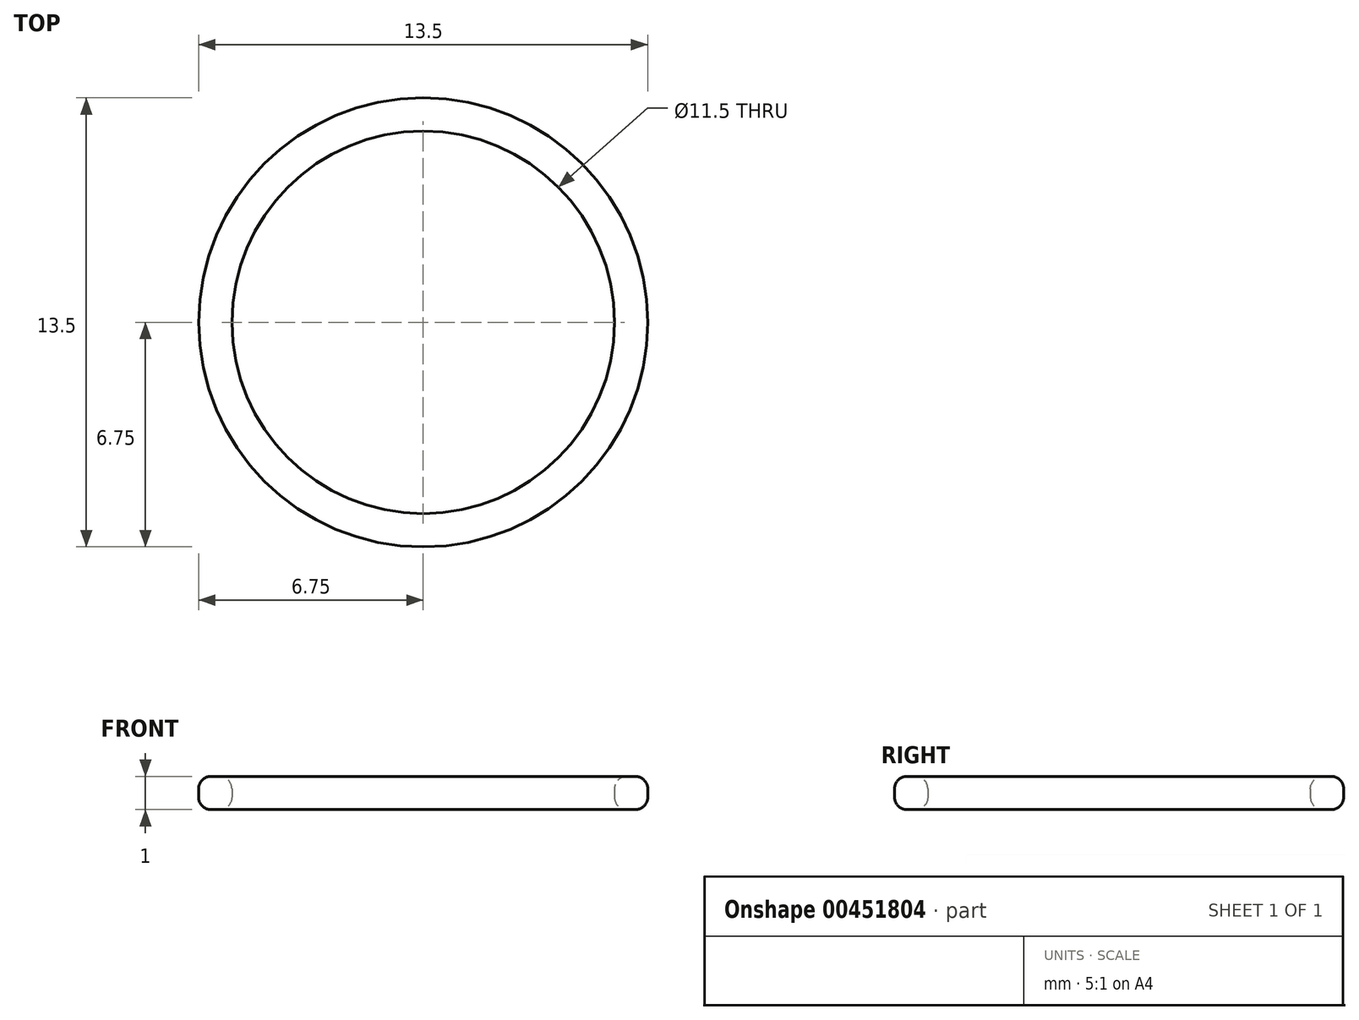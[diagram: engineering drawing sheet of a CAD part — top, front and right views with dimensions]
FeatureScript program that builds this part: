
annotation { "Feature Type Name" : "Feature", "Feature Type Description" : "" }
export const myFeature = defineFeature(function(context is Context, id is Id, definition is map)
    precondition{}
    {
        {
            var Q0;
            Q0=qCreatedBy(makeId("Top.planeOp"),FACE);
            var sketch = newSketch(context, id + "F0", { "sketchPlane" : qUnion([Q0])});
            skCircle(sketch, "E0", {"center": v(0, 0) * mm, "radius": 6.75 * mm});
            skCircle(sketch, "E1", {"center": v(0, 0) * mm, "radius": 5.75 * mm});
            skSolve(sketch);
        }
        {
            var Q0;
            Q0=qSketchRegion(id+"F0",true);
            extrude(context, id + "F1", {"entities" : qUnion([Q0]), "depth" : 1 * mm, "offsetDistance" : 25 * mm});
        }
        {
            var Q0;
            Q0=makeQuery(id+"F1.opExtrude","CAP_EDGE",EDGE,{"disambiguationData":[OSD([sQuery(id+"F0.wireOp",EDGE,"E1")])],"isStart":false});
            var Q1;
            Q1=makeQuery(id+"F1.opExtrude","CAP_EDGE",EDGE,{"disambiguationData":[OSD([sQuery(id+"F0.wireOp",EDGE,"E0")])],"isStart":false});
            var Q2;
            Q2=makeQuery(id+"F1.opExtrude","CAP_EDGE",EDGE,{"disambiguationData":[OSD([sQuery(id+"F0.wireOp",EDGE,"E0")])],"isStart":true});
            var Q3;
            Q3=makeQuery(id+"F1.opExtrude","CAP_EDGE",EDGE,{"disambiguationData":[OSD([sQuery(id+"F0.wireOp",EDGE,"E1")])],"isStart":true});
            fillet(context, id + "F2", {"entities" : qUnion([Q0, Q1, Q2, Q3]), "radius" : 0.38 * mm, "tangentPropagation" : true, "allowEdgeOverflow" : false});
        }
    });
